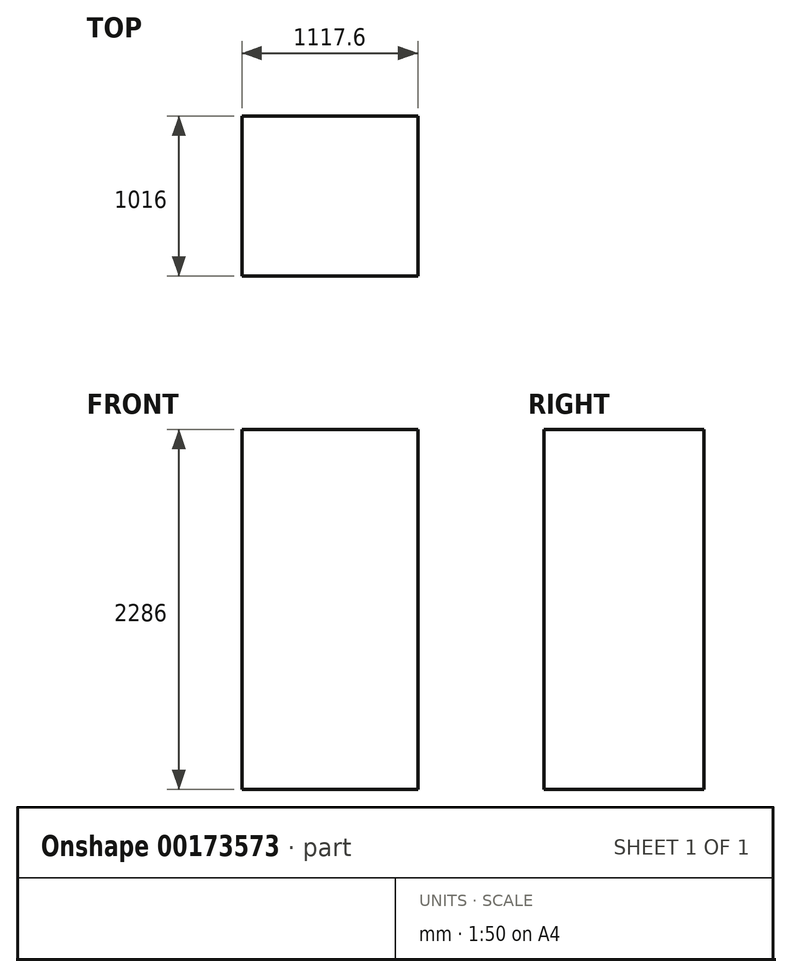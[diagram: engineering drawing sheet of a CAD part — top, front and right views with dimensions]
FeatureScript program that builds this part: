
annotation { "Feature Type Name" : "Feature", "Feature Type Description" : "" }
export const myFeature = defineFeature(function(context is Context, id is Id, definition is map)
    precondition{}
    {
        {
            var Q0;
            Q0=qCreatedBy(makeId("Front.planeOp"),FACE);
            var sketch = newSketch(context, id + "F0", { "sketchPlane" : qUnion([Q0])});
            skLineSegment(sketch, "E0.bottom", {"start": v(558.8, 1143) * mm, "end": v(-558.8, 1143) * mm});
            skLineSegment(sketch, "E0.top", {"start": v(558.8, -1143) * mm, "end": v(-558.8, -1143) * mm});
            skLineSegment(sketch, "E0.left", {"start": v(558.8, 1143) * mm, "end": v(558.8, -1143) * mm});
            skLineSegment(sketch, "E0.right", {"start": v(-558.8, 1143) * mm, "end": v(-558.8, -1143) * mm});
            skPoint(sketch, "E0.middle", {"position": v(0, 0) * mm});
            skSolve(sketch);
        }
        {
            var Q0;
            Q0 = qSketchRegion(id + "F0", true);
            extrude(context, id + "F1", {"entities" : qUnion([Q0]), "depth" : 1016 * mm});
        }
    });
